# Revit family: Plumbing_Valves_Zurn_ZEMS6152_Wall-Mounted_Final
name_source: partatom
category: Plumbing Fixtures
units: mm (PartAtom-declared; Revit-internal decimal feet)

## family parameters
Cut with Voids When Loaded = No
Host = Face
Maintain Annotation Orientation = No
OmniClass Number = 23.65.00.00
OmniClass Title = Supply and Distribution of Liquids and Gases
Part Type = Normal
Room Calculation Point = No
Round Connector Dimension = Use Radius
Shared = No

## types (4) — shared parameters
Activation Method = Sensor Operated
Assembly Code = D2060.10
CW Connection = Yes
CWFU = 1
Centerline of Flush valve to wall = 3.75 "
Centerline of Stop Valve to Centerline of Flush Valve = 4.75 "
Default Elevation = 48 "
Description = AquaSense® Hardwired Automatic Sensor Valve for Water Closets
HW Connection = No
Inlet Connection Size (Inch) = 1 "
Main Material = Vitreous China - Zurn - White
Manufacturer = Zurn Water, LLC
Manufacturer Brand = Zurn
Model = ZEMS6152AV
Modified Date = 01/25/2026
Product Documentation Link = https://files.zurn.com
Product Installation Sheet URL = https://files.zurn.com
Product Page URL = https://www.zurn.com
Product data URL = https://bimobject.com
Repair Parts URL = https://files.zurn.com
URL = www.zurn.com
Valve Height = 14.5 "
Vent Connection = No
Waste Connection = No
zero-valued in all types: HWFU, WFU

## per-type parameters (varying)
| type | Flush Rate (GPF) | Type Comments |
| ZEMS6152AV (3.5 GPF) | 3.50 GPF | ZEMS6152AV (3.5 GPF) |
| ZEMS6152AV-ONE (1.1 GPF) | 1.1 GPF | ZEMS6152AV-ONE (1.1 GPF) |
| ZEMS6152AV-WS1 (1.6 GPF) | 1.6 GPF | ZEMS6152AV-WS1 (1.6 GPF) |
| ZEMS6152AV-HET (1.28 GPF) | 1.28 GPF | ZEMS6152AV-ONE (1.1 GPF) |

## geometry (parser evidence)
native form markers: Blend x4, Sweep x4
no freeform markers — native parametric forms only
